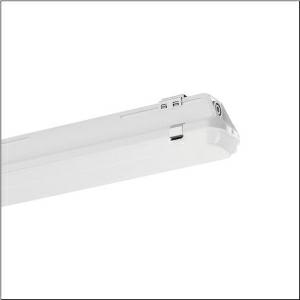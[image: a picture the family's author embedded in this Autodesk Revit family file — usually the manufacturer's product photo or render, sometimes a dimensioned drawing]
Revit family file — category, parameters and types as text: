
# Revit family: monsun_11_facade_51ff40dp460l007
name_source: partatom
category: Lighting Fixtures
units: mm (PartAtom-declared; Revit-internal decimal feet)

## family parameters
Cut with Voids When Loaded = No
Host = Face
Light Source = No
Part Type = Normal
Room Calculation Point = No
Round Connector Dimension = Use Diameter
Shared = No

## types (1)
- --- (1 x LED, 6190 lm, 31.8 W, 4000K)
    Apparent Load = 32 VA
    CIE Flux Codes = 47 77 93 95 100
    Color Rendering = 80
    Color Temperature = 4000K
    Default Elevation = 1800 mm
    Description = Monsun 11 facade, damp-proof luminaire, chain hanger, primary optical cover: enclosure, of PMMA, light emission: direct distribution, primary light characteristic: symmetric, installation type: surface-mounted, horizontal mounting, vertical mounting, LED, rated luminous flux: 6.190lm, luminous efficacy: 195lm/W, light colour: 840, colour temperature: 4000K, control gear: DALI 2, with terminal, 5-pole, max. 2.5mm², through-wiring: 7x 2.5mm², mains connection: 220..240V, AC, 50/60Hz, rated input power: 32W, housing, of glass-fibre reinforced polyester, uncoated, bright grey, incl. chain hanger, for cables, Ø 8.4..12mm, with climate membrane, length: 1.590mm, width: 90mm, height: 88mm, clip for enclosure, of stainless steel (V2A), ceiling mounting element, of stainless steel (V2A), chain hanger, of stainless steel (V2A), protection rating (complete): IP66, insulation class (complete): insulation class I (protective earthing), certification: CE, ENEC, VDE, UKCA, protection symbol: D, impact resistance: IK06, permissible operating ambient temperature: -25..+30°C, standard: EN 50419, EN 60598-2-1, contact your sales advisor before using the luminaires in applications with unclear chemical exposure, large temperature fluctuations or condensation-forming humidity, LABS conformity tested according to VDMA 24364:2018-05, exposed outdoor area, packaging unit: 1 piece
    Height = 89 mm
    Lamp = 1 x LED
    Lamp Light Flux = 6190 lm
    Lamp Power = 31.8 W
    Lamp count = 1
    Length = 1590 mm
    Luminous efficacy = 195 lm/W
    Manufacturer = Siteco
    ModVariant = No
    Model = 51FF40DP460L007
    Mounting Place = Ceiling
    Mounting Type = Surface mounted
    Number of Poles = 1
    OnlyDefault = Yes
    Power Factor = 1
    Product Name = Monsun 11 facade
    Product group = damp-proof luminaire
    ProductGroupID = 300
    Protection Class = Protection class I
    Protection Degree = IP 66
    RLX_Detail_Level = 1
    RLX_Emergency_Light_Flux = 0 lm
    RLX_Emergency_Type = 0
    RLX_Emergency_Type_DB = No
    RlxData = <blob elided: 92017 chars, md5=b778663d>
    Socket = socket
    Standby Power = 0 W
    System Light Flux = 6190 lm
    System Power = 32 W
    Type Comments = factory setting: luminous flux: 100 % | dim-lin: 254 | 221 mA
    Type Image = l_1349237.jpg
    URL = http://relux.com
    VarID = @adj_034297
    Voltage = 0 V
    Weight = 0.00 kg
    Width = 90 mm

## geometry (parser evidence)
native form markers: Blend x4, Sweep x13
no freeform markers — native parametric forms only
